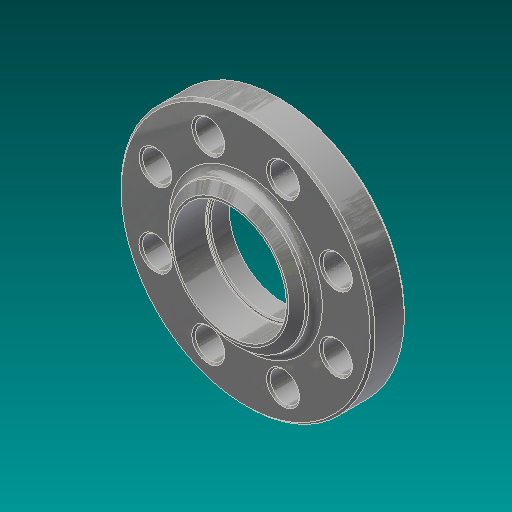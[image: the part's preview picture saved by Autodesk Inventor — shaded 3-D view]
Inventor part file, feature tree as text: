
AUTODESK INVENTOR PART (.ipt)
format: ipt  version: 2017.3 (Build 213256000, 256)  size: 272,896 bytes
history: native  units: in
note: dims shown in document units (in); Inventor stores cm internally (conversion verified against a paired STEP export)
features: chamfer x3, sketch x3, revolve x1, hole x1, pattern_circular x1, extrude x1, fillet x1
ambient origin geometry x8: Origin, YZ Plane, XZ Plane, XY Plane, X Axis, Y Axis, Z Axis, Center Point
bodies: Solid1 (feature_tree)
feature tree (11):
  revolve  "Revolution1"  [1 undecoded]
  hole  "Hole1"  [1 undecoded]
  chamfer  "Chamfer1"  Distance=3.5in
  pattern_circular  "Circular Pattern1"  [2 undecoded]
  chamfer  "Chamfer2"  Distance=3.61in
  extrude  "Extrusion1"  Depth=0.0312in
  fillet  "Fillet1"  Radius=0.2375in
  chamfer  "Chamfer3"  Distance=0.2in
  sketch  "Sketch1"  dims[d0=1.3438in d1=6.5in]
  sketch  "Sketch2"  dims[d2=0.9375in d3=3.625in]
  sketch  "Sketch3"  dims[d4=0.0625in d5=3.5in d6=2.9in d7=3.61in d8=0.2577in d9=0.2375in d10=0.2in d11=90.0deg d12=5.0in d13=22.5deg d14=0.75in d15=0.75in d16=0.375in d17=0.25in d18=0.5635in d19=1.0in d20=0.8108in d21=0.0469in d22=0.125in d23=45.0deg d24=3.1496in d25=360.0deg d27=0.0625in d28=0.125in d29=45.0deg d30=2.7125in d31=0.5in d32=0.0in d33=0.0156in d34=0.0312in d35=0.125in d36=45.0deg]
note: 4 required parameter values undecoded (feature->parameter linkage not recoverable at this tier; creation-order binding heuristic only, values carry confidence <= 0.55)